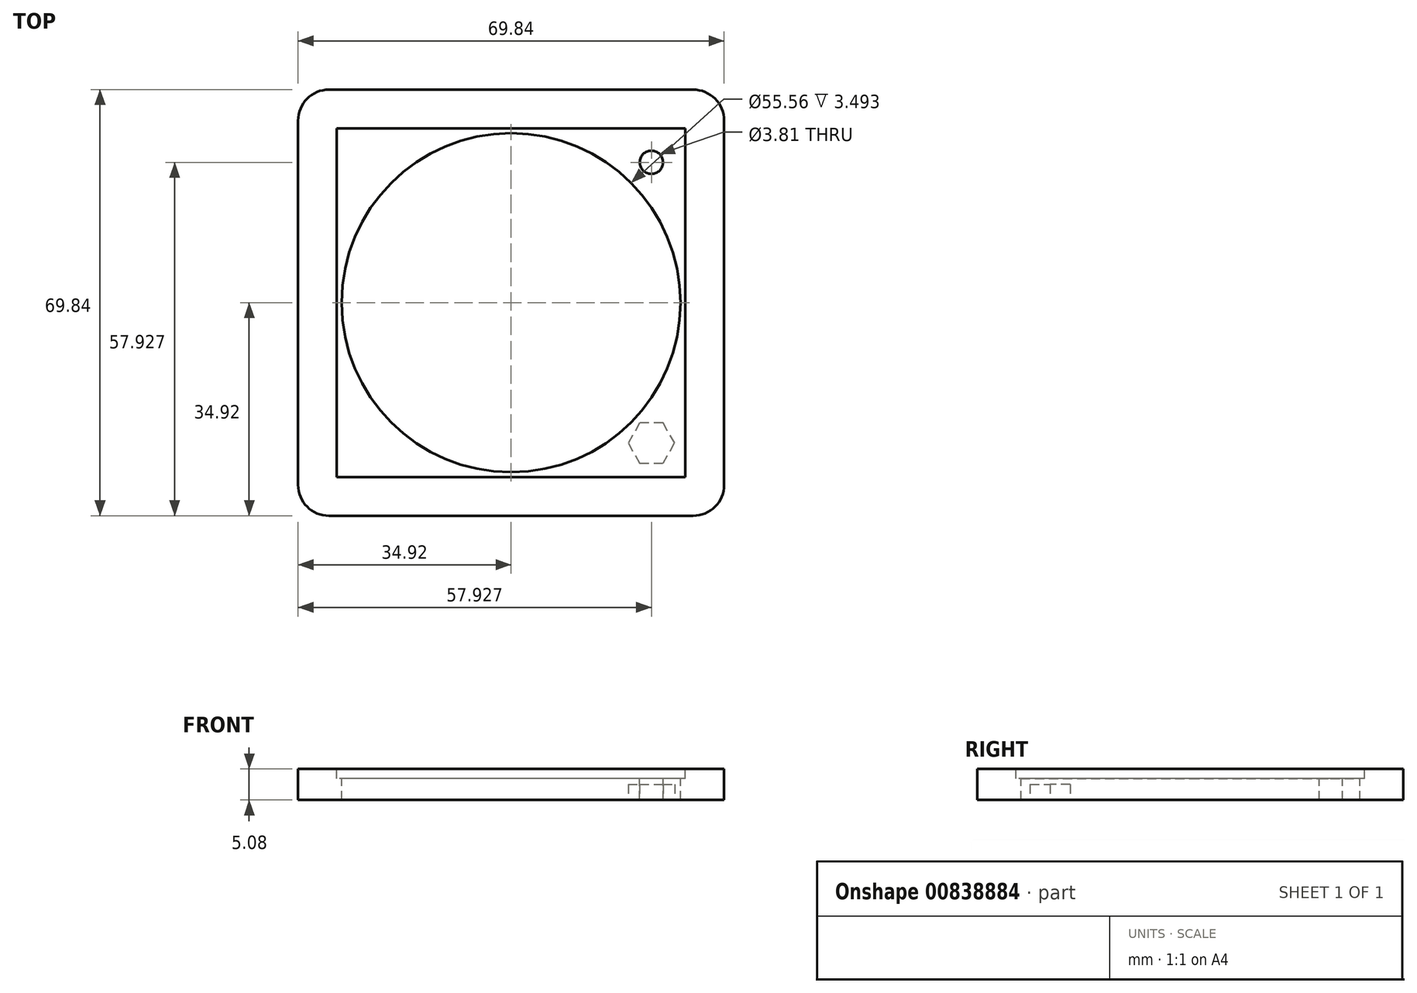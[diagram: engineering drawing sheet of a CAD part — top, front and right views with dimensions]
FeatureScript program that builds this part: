
annotation { "Feature Type Name" : "Feature", "Feature Type Description" : "" }
export const myFeature = defineFeature(function(context is Context, id is Id, definition is map)
    precondition{}
    {
        {
            var Q0;
            Q0=qCreatedBy(makeId("Top.planeOp"),FACE);
            var sketch = newSketch(context, id + "F0", { "sketchPlane" : qUnion([Q0])});
            skLineSegment(sketch, "E0.bottom", {"start": v(34.92, 34.93) * mm, "end": v(-34.93, 34.93) * mm});
            skLineSegment(sketch, "E0.top", {"start": v(34.93, -34.93) * mm, "end": v(-34.92, -34.93) * mm});
            skLineSegment(sketch, "E0.left", {"start": v(34.92, 34.93) * mm, "end": v(34.93, -34.93) * mm});
            skLineSegment(sketch, "E0.right", {"start": v(-34.93, 34.93) * mm, "end": v(-34.92, -34.93) * mm});
            skPoint(sketch, "E0.middle", {"position": v(0, 0) * mm});
            skSolve(sketch);
        }
        {
            var Q0;
            Q0=makeQuery(id+"F0.imprint","IMPRINT",FACE,{"disambiguationData":[TD([[makeQuery(id+"F0.imprint","IMPRINT",EDGE,{"derivedFrom":sQuery(id+"F0.wireOp",EDGE,"E0.bottom")}),1.0]])]});
            extrude(context, id + "F1", {"entities" : qUnion([Q0]), "depth" : 5.08 * mm, "offsetDistance" : 25.4 * mm});
        }
        {
            var Q0;
            Q0=makeQuery(id+"F1.opExtrude","SWEPT_EDGE",EDGE,{"disambiguationData":[OSD([sQuery(id+"F0.wireOp",EDGE,"E0.top"),sQuery(id+"F0.wireOp",EDGE,"E0.right")])]});
            var Q1;
            Q1=makeQuery(id+"F1.opExtrude","SWEPT_EDGE",EDGE,{"disambiguationData":[OSD([sQuery(id+"F0.wireOp",EDGE,"E0.top"),sQuery(id+"F0.wireOp",EDGE,"E0.left")])]});
            var Q2;
            Q2=makeQuery(id+"F1.opExtrude","SWEPT_EDGE",EDGE,{"disambiguationData":[OSD([sQuery(id+"F0.wireOp",EDGE,"E0.bottom"),sQuery(id+"F0.wireOp",EDGE,"E0.left")])]});
            var Q3;
            Q3=makeQuery(id+"F1.opExtrude","SWEPT_EDGE",EDGE,{"disambiguationData":[OSD([sQuery(id+"F0.wireOp",EDGE,"E0.bottom"),sQuery(id+"F0.wireOp",EDGE,"E0.right")])]});
            fillet(context, id + "F2", {"entities" : qUnion([Q0, Q1, Q2, Q3]), "radius" : 5.08 * mm, "tangentPropagation" : true, "allowEdgeOverflow" : false});
        }
        {
            var Q0;
            Q0=makeQuery(id+"F1.opExtrude","CAP_FACE",FACE,{"disambiguationData":[OSD([sQuery(id+"F0.wireOp",EDGE,"E0.bottom"),sQuery(id+"F0.wireOp",EDGE,"E0.top"),sQuery(id+"F0.wireOp",EDGE,"E0.left"),sQuery(id+"F0.wireOp",EDGE,"E0.right")])],"isStart":false});
            var sketch = newSketch(context, id + "F3", { "sketchPlane" : qUnion([Q0])});
            skCircle(sketch, "E1", {"center": v(0, 0) * mm, "radius": 27.78 * mm});
            skSolve(sketch);
        }
        {
            var Q0;
            Q0 = qSketchRegion(id + "F3", true);
            var Q1;
            Q1=makeQuery(id+"F1.opExtrude","CAP_FACE",FACE,{"disambiguationData":[OSD([sQuery(id+"F0.wireOp",EDGE,"E0.bottom"),sQuery(id+"F0.wireOp",EDGE,"E0.top"),sQuery(id+"F0.wireOp",EDGE,"E0.left"),sQuery(id+"F0.wireOp",EDGE,"E0.right")])],"isStart":true});
            extrude(context, id + "F4", {"entities" : qUnion([Q0]), "operationType" : NewBodyOperationType.REMOVE, "endBound" : BoundingType.UP_TO_SURFACE, "oppositeDirection" : true, "depth" : 25.4 * mm, "endBoundEntityFace" : qUnion([Q1]), "offsetDistance" : 25.4 * mm});
        }
        {
            var Q0;
            Q0=makeQuery(id+"F1.opExtrude","CAP_FACE",FACE,{"disambiguationData":[OSD([sQuery(id+"F0.wireOp",EDGE,"E0.bottom"),sQuery(id+"F0.wireOp",EDGE,"E0.top"),sQuery(id+"F0.wireOp",EDGE,"E0.left"),sQuery(id+"F0.wireOp",EDGE,"E0.right")])],"isStart":false});
            var sketch = newSketch(context, id + "F5", { "sketchPlane" : qUnion([Q0])});
            skLineSegment(sketch, "E2.bottom", {"start": v(28.58, 28.58) * mm, "end": v(-28.57, 28.58) * mm});
            skLineSegment(sketch, "E2.top", {"start": v(28.57, -28.58) * mm, "end": v(-28.58, -28.58) * mm});
            skLineSegment(sketch, "E2.left", {"start": v(28.58, 28.58) * mm, "end": v(28.57, -28.58) * mm});
            skLineSegment(sketch, "E2.right", {"start": v(-28.57, 28.58) * mm, "end": v(-28.58, -28.58) * mm});
            skPoint(sketch, "E2.middle", {"position": v(0, 0) * mm});
            skSolve(sketch);
        }
        {
            var Q0;
            Q0 = qSketchRegion(id + "F5", true);
            extrude(context, id + "F6", {"entities" : qUnion([Q0]), "operationType" : NewBodyOperationType.REMOVE, "oppositeDirection" : true, "depth" : 1.59 * mm, "offsetDistance" : 25.4 * mm});
        }
        {
            var Q0;
            Q0=makeQuery(id+"F6.boolean.opBoolean","COPY",FACE,{"derivedFrom":makeQuery(id+"F6.opExtrude","CAP_FACE",FACE,{"disambiguationData":[OSD([sQuery(id+"F5.wireOp",EDGE,"E2.bottom"),sQuery(id+"F5.wireOp",EDGE,"E2.top"),sQuery(id+"F5.wireOp",EDGE,"E2.left"),sQuery(id+"F5.wireOp",EDGE,"E2.right")])],"isStart":false})});
            var sketch = newSketch(context, id + "F7", { "sketchPlane" : qUnion([Q0])});
            skLineSegment(sketch, "E3", {"start": v(28.58, 28.58) * mm, "end": v(19.64, 19.64) * mm});
            skCircle(sketch, "E4", {"center": v(23, 23) * mm, "radius": 1.9 * mm});
            skSolve(sketch);
        }
        {
            var Q0;
            {var subQ0=sQuery(id+"F7.wireOp",EDGE,"E4");var subQ1=sQuery(id+"F7.wireOp",EDGE,"E3");var subQ2=makeQuery(id+"F7.imprint","INTERSECT",VERTEX,{"disambiguationData":[OD(0.0)],"derivedFrom":[subQ1,subQ0]});Q0=makeQuery(id+"F7.imprint","IMPRINT",FACE,{"disambiguationData":[TD([[makeQuery(id+"F7.imprint","IMPRINT",EDGE,{"disambiguationData":[TD([[subQ2,1.0]])],"derivedFrom":subQ1}),-1.0]])]});}
            var Q1;
            {var subQ0=sQuery(id+"F7.wireOp",EDGE,"E4");var subQ1=sQuery(id+"F7.wireOp",EDGE,"E3");var subQ2=makeQuery(id+"F7.imprint","INTERSECT",VERTEX,{"disambiguationData":[OD(0.0)],"derivedFrom":[subQ1,subQ0]});Q1=makeQuery(id+"F7.imprint","IMPRINT",FACE,{"disambiguationData":[TD([[makeQuery(id+"F7.imprint","IMPRINT",EDGE,{"disambiguationData":[TD([[subQ2,1.0]])],"derivedFrom":subQ1}),1.0]])]});}
            var Q2;
            Q2=makeQuery(id+"F1.opExtrude","CAP_FACE",FACE,{"disambiguationData":[OSD([sQuery(id+"F0.wireOp",EDGE,"E0.bottom"),sQuery(id+"F0.wireOp",EDGE,"E0.top"),sQuery(id+"F0.wireOp",EDGE,"E0.left"),sQuery(id+"F0.wireOp",EDGE,"E0.right")])],"isStart":true});
            extrude(context, id + "F8", {"entities" : qUnion([Q0, Q1]), "operationType" : NewBodyOperationType.REMOVE, "endBound" : BoundingType.UP_TO_SURFACE, "oppositeDirection" : true, "depth" : 25.4 * mm, "endBoundEntityFace" : qUnion([Q2]), "offsetDistance" : 25.4 * mm});
        }
        {
            var Q0;
            Q0=qCreatedBy(makeId("Front.planeOp"),FACE);
            var sketch = newSketch(context, id + "F9", { "sketchPlane" : qUnion([Q0])});
            skLineSegment(sketch, "E5", {"start": v(0, 79.43) * mm, "end": v(0, -44.4) * mm});
            skSolve(sketch);
        }
        {
            var Q0;
            Q0=makeQuery(id+"F1.opExtrude","CAP_FACE",FACE,{"disambiguationData":[OSD([sQuery(id+"F0.wireOp",EDGE,"E0.bottom"),sQuery(id+"F0.wireOp",EDGE,"E0.top"),sQuery(id+"F0.wireOp",EDGE,"E0.left"),sQuery(id+"F0.wireOp",EDGE,"E0.right")])],"isStart":true});
            var sketch = newSketch(context, id + "F10", { "sketchPlane" : qUnion([Q0])});
            skCircle(sketch, "E6.cCircle", {"center": v(23, 23) * mm, "radius": 3.3 * mm, "construction": true});
            skLineSegment(sketch, "E6.0", {"start": v(24.91, 26.3) * mm, "end": v(26.82, 23) * mm});
            skLineSegment(sketch, "E6.1", {"start": v(26.82, 23) * mm, "end": v(24.91, 19.7) * mm});
            skLineSegment(sketch, "E6.2", {"start": v(24.91, 19.7) * mm, "end": v(21.1, 19.7) * mm});
            skLineSegment(sketch, "E6.3", {"start": v(21.1, 19.7) * mm, "end": v(19.2, 23) * mm});
            skLineSegment(sketch, "E6.4", {"start": v(19.2, 23) * mm, "end": v(21.1, 26.3) * mm});
            skLineSegment(sketch, "E6.5", {"start": v(21.1, 26.3) * mm, "end": v(24.91, 26.3) * mm});
            skPoint(sketch, "E6.0.midPoint", {"position": v(25.86, 24.66) * mm});
            skSolve(sketch);
        }
        {
            var Q0;
            Q0 = qSketchRegion(id + "F10", true);
            extrude(context, id + "F11", {"entities" : qUnion([Q0]), "operationType" : NewBodyOperationType.REMOVE, "oppositeDirection" : true, "depth" : 2.54 * mm, "offsetDistance" : 25.4 * mm});
        }
    });
